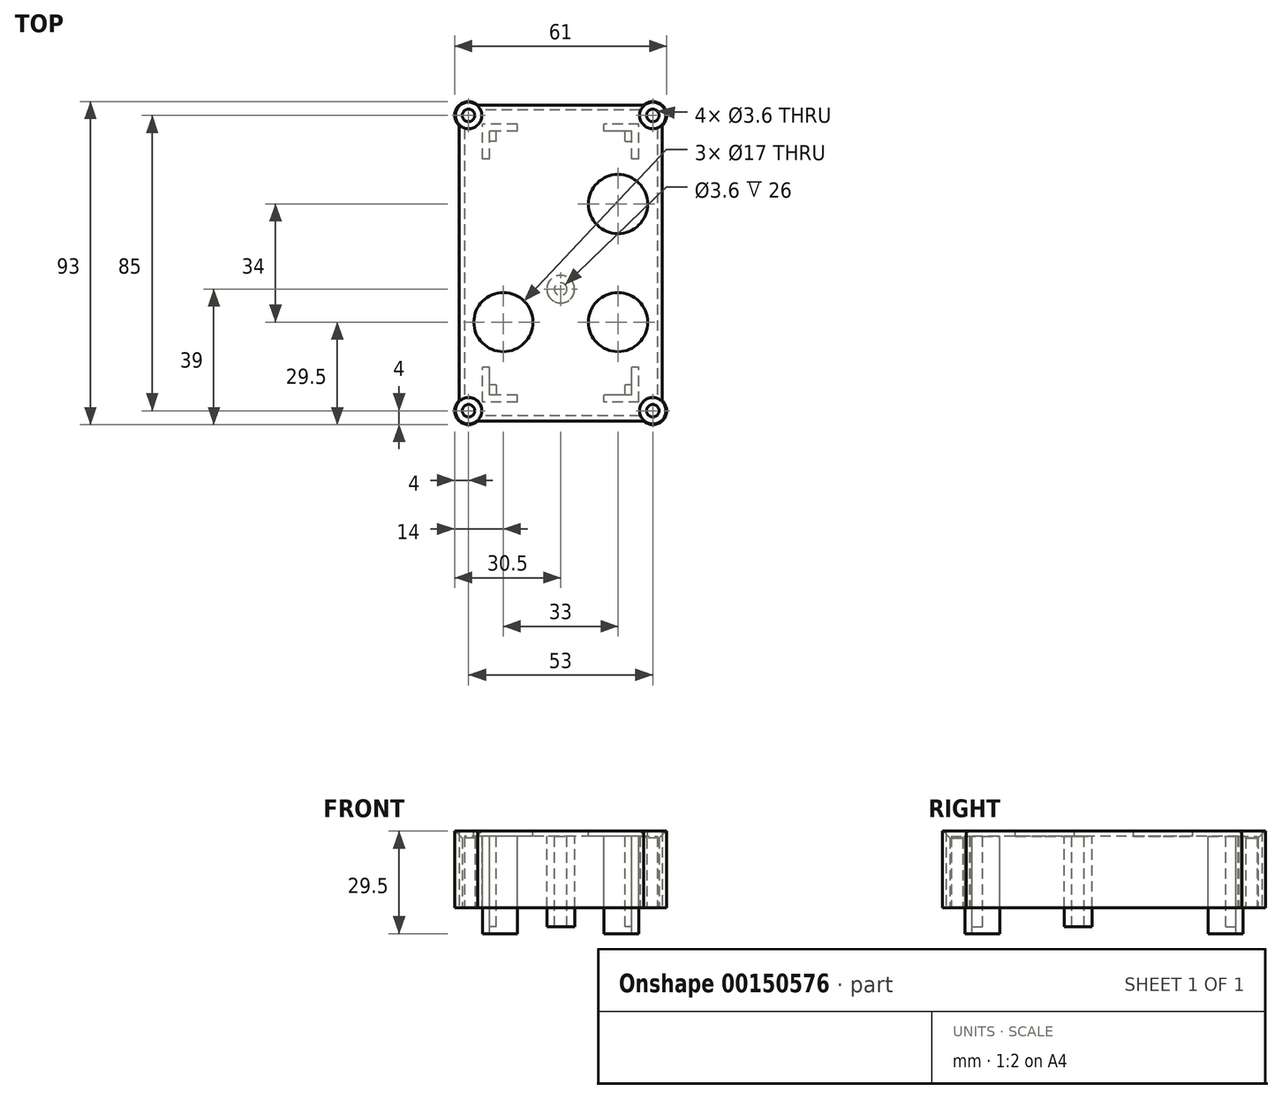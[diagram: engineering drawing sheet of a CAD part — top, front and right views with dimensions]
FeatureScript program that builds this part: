
annotation { "Feature Type Name" : "Feature", "Feature Type Description" : "" }
export const myFeature = defineFeature(function(context is Context, id is Id, definition is map)
    precondition{}
    {
        {
            var Q0;
            Q0=qCreatedBy(makeId("Top.planeOp"),FACE);
            var sketch = newSketch(context, id + "F0", { "sketchPlane" : qUnion([Q0])});
            skLineSegment(sketch, "E0.bottom", {"start": v(29.25, 45.5) * mm, "end": v(-29.25, 45.5) * mm});
            skLineSegment(sketch, "E0.top", {"start": v(29.25, -45.5) * mm, "end": v(-29.25, -45.5) * mm});
            skLineSegment(sketch, "E0.left", {"start": v(29.25, 45.5) * mm, "end": v(29.25, -45.5) * mm});
            skLineSegment(sketch, "E0.right", {"start": v(-29.25, 45.5) * mm, "end": v(-29.25, -45.5) * mm});
            skPoint(sketch, "E0.middle", {"position": v(0, 0) * mm});
            skSolve(sketch);
        }
        {
            var Q0;
            Q0=qSketchRegion(id+"F0",true);
            extrude(context, id + "F1", {"entities" : qUnion([Q0]), "depth" : 22 * mm});
        }
        {
            var Q0;
            Q0=makeQuery(id+"F1.opExtrude","CAP_FACE",FACE,{"disambiguationData":[OSD([sQuery(id+"F0.wireOp",EDGE,"E0.bottom"),sQuery(id+"F0.wireOp",EDGE,"E0.top"),sQuery(id+"F0.wireOp",EDGE,"E0.left"),sQuery(id+"F0.wireOp",EDGE,"E0.right")])],"isStart":true});
            shell(context, id + "F2", {"entities" : qUnion([Q0]), "thickness" : 1.5 * mm});
        }
        {
            var Q0;
            Q0=makeQuery(id+"F1.opExtrude","CAP_FACE",FACE,{"disambiguationData":[OSD([sQuery(id+"F0.wireOp",EDGE,"E0.bottom"),sQuery(id+"F0.wireOp",EDGE,"E0.top"),sQuery(id+"F0.wireOp",EDGE,"E0.left"),sQuery(id+"F0.wireOp",EDGE,"E0.right")])],"isStart":false});
            var sketch = newSketch(context, id + "F3", { "sketchPlane" : qUnion([Q0])});
            skCircle(sketch, "E1", {"center": v(16.5, 17) * mm, "radius": 8.5 * mm});
            skCircle(sketch, "E2.MirrorC", {"center": v(16.5, -17) * mm, "radius": 8.5 * mm});
            skCircle(sketch, "E3.MirrorC", {"center": v(-16.5, -17) * mm, "radius": 8.5 * mm});
            skCircle(sketch, "E4", {"center": v(16.5, -17) * mm, "radius": 11 * mm, "construction": true});
            skCircle(sketch, "E5", {"center": v(-16.5, -17) * mm, "radius": 11 * mm, "construction": true});
            skCircle(sketch, "E6", {"center": v(16.5, 17) * mm, "radius": 11 * mm, "construction": true});
            skSolve(sketch);
        }
        {
            var Q0;
            Q0=qSketchRegion(id+"F3",true);
            extrude(context, id + "F4", {"entities" : qUnion([Q0]), "operationType" : NewBodyOperationType.REMOVE, "oppositeDirection" : true, "depth" : 25 * mm});
        }
        {
            var Q0;
            Q0=makeQuery(id+"F1.opExtrude","SWEPT_EDGE",EDGE,{"disambiguationData":[OSD([sQuery(id+"F0.wireOp",EDGE,"E0.bottom"),sQuery(id+"F0.wireOp",EDGE,"E0.right")])]});
            var Q1;
            Q1=makeQuery(id+"F1.opExtrude","SWEPT_EDGE",EDGE,{"disambiguationData":[OSD([sQuery(id+"F0.wireOp",EDGE,"E0.bottom"),sQuery(id+"F0.wireOp",EDGE,"E0.left")])]});
            var Q2;
            Q2=makeQuery(id+"F1.opExtrude","SWEPT_EDGE",EDGE,{"disambiguationData":[OSD([sQuery(id+"F0.wireOp",EDGE,"E0.top"),sQuery(id+"F0.wireOp",EDGE,"E0.right")])]});
            var Q3;
            Q3=makeQuery(id+"F1.opExtrude","SWEPT_EDGE",EDGE,{"disambiguationData":[OSD([sQuery(id+"F0.wireOp",EDGE,"E0.top"),sQuery(id+"F0.wireOp",EDGE,"E0.left")])]});
            fillet(context, id + "F5", {"entities" : qUnion([Q0, Q1, Q2, Q3]), "radius" : 3 * mm, "tangentPropagation" : true, "allowEdgeOverflow" : false});
        }
        {
            var Q0;
            Q0=makeQuery(id+"F2.opShell","OFFSET_EDGE",EDGE,{"disambiguationData":[OSD([sQuery(id+"F0.wireOp",EDGE,"E0.bottom"),sQuery(id+"F0.wireOp",EDGE,"E0.right")])]});
            var Q1;
            Q1=makeQuery(id+"F2.opShell","OFFSET_EDGE",EDGE,{"disambiguationData":[OSD([sQuery(id+"F0.wireOp",EDGE,"E0.top"),sQuery(id+"F0.wireOp",EDGE,"E0.right")])]});
            var Q2;
            Q2=makeQuery(id+"F2.opShell","OFFSET_EDGE",EDGE,{"disambiguationData":[OSD([sQuery(id+"F0.wireOp",EDGE,"E0.top"),sQuery(id+"F0.wireOp",EDGE,"E0.left")])]});
            var Q3;
            Q3=makeQuery(id+"F2.opShell","OFFSET_EDGE",EDGE,{"disambiguationData":[OSD([sQuery(id+"F0.wireOp",EDGE,"E0.bottom"),sQuery(id+"F0.wireOp",EDGE,"E0.left")])]});
            fillet(context, id + "F6", {"entities" : qUnion([Q0, Q1, Q2, Q3]), "radius" : 2 * mm, "tangentPropagation" : true, "allowEdgeOverflow" : false});
        }
        {
            var Q0;
            Q0=makeQuery(id+"F2.opShell","OFFSET_FACE",FACE,{"disambiguationData":[OSD([sQuery(id+"F0.wireOp",EDGE,"E0.bottom"),sQuery(id+"F0.wireOp",EDGE,"E0.top"),sQuery(id+"F0.wireOp",EDGE,"E0.left"),sQuery(id+"F0.wireOp",EDGE,"E0.right")])]});
            var sketch = newSketch(context, id + "F7", { "sketchPlane" : qUnion([Q0])});
            skLineSegment(sketch, "E7.bottom", {"start": v(20.5, 38) * mm, "end": v(12.5, 38) * mm});
            skLineSegment(sketch, "E7.top", {"start": v(20.5, -38) * mm, "end": v(12.5, -38) * mm});
            skLineSegment(sketch, "E7.left", {"start": v(20.5, 38) * mm, "end": v(20.5, 30) * mm});
            skLineSegment(sketch, "E7.right", {"start": v(-20.5, 38) * mm, "end": v(-20.5, 30) * mm});
            skPoint(sketch, "E7.middle", {"position": v(0, 0) * mm});
            skLineSegment(sketch, "E8.bottom", {"start": v(22.5, 40) * mm, "end": v(12.5, 40) * mm});
            skLineSegment(sketch, "E8.top", {"start": v(22.5, -40) * mm, "end": v(12.5, -40) * mm});
            skLineSegment(sketch, "E8.left", {"start": v(22.5, 40) * mm, "end": v(22.5, 30) * mm});
            skLineSegment(sketch, "E8.right", {"start": v(-22.5, 40) * mm, "end": v(-22.5, 30) * mm});
            skLineSegment(sketch, "E9", {"start": v(12.5, 40) * mm, "end": v(12.5, 38) * mm});
            skLineSegment(sketch, "E10", {"start": v(-12.5, 40) * mm, "end": v(-12.5, 38) * mm});
            skLineSegment(sketch, "E11", {"start": v(22.5, 30) * mm, "end": v(20.5, 30) * mm});
            skLineSegment(sketch, "E12", {"start": v(22.5, -30) * mm, "end": v(20.5, -30) * mm});
            skLineSegment(sketch, "E13.trimOffspring", {"start": v(12.5, -38) * mm, "end": v(12.5, -40) * mm});
            skLineSegment(sketch, "E14.trimOffspring", {"start": v(20.5, -30) * mm, "end": v(20.5, -38) * mm});
            skLineSegment(sketch, "E15.trimOffspring", {"start": v(22.5, -30) * mm, "end": v(22.5, -40) * mm});
            skLineSegment(sketch, "E16.trimOffspring", {"start": v(-12.5, -38) * mm, "end": v(-20.5, -38) * mm});
            skLineSegment(sketch, "E17.trimOffspring", {"start": v(-12.5, -40) * mm, "end": v(-22.5, -40) * mm});
            skLineSegment(sketch, "E18.trimOffspring", {"start": v(-12.5, -38) * mm, "end": v(-12.5, -40) * mm});
            skLineSegment(sketch, "E19.trimOffspring", {"start": v(-20.5, -30) * mm, "end": v(-22.5, -30) * mm});
            skLineSegment(sketch, "E20.trimOffspring", {"start": v(-20.5, -30) * mm, "end": v(-20.5, -38) * mm});
            skLineSegment(sketch, "E21.trimOffspring", {"start": v(-22.5, -30) * mm, "end": v(-22.5, -40) * mm});
            skLineSegment(sketch, "E22.trimOffspring", {"start": v(-20.5, 30) * mm, "end": v(-22.5, 30) * mm});
            skLineSegment(sketch, "E23.trimOffspring", {"start": v(-12.5, 38) * mm, "end": v(-20.5, 38) * mm});
            skLineSegment(sketch, "E24.trimOffspring", {"start": v(-12.5, 40) * mm, "end": v(-22.5, 40) * mm});
            skSolve(sketch);
        }
        {
            var Q0;
            Q0=qSketchRegion(id+"F7",true);
            extrude(context, id + "F8", {"entities" : qUnion([Q0]), "operationType" : NewBodyOperationType.ADD, "depth" : 28 * mm});
        }
        {
            var Q0;
            Q0=makeQuery(id+"F7.imprint","IMPRINT",FACE,{"disambiguationData":[TD([[makeQuery(id+"F7.imprint","IMPRINT",EDGE,{"derivedFrom":sQuery(id+"F7.wireOp",EDGE,"E7.bottom")}),1.0]])]});
            var sketch = newSketch(context, id + "F9", { "sketchPlane" : qUnion([Q0])});
            skCircle(sketch, "E25", {"center": v(0, 7.5) * mm, "radius": 2 * mm, "construction": true});
            skLineSegment(sketch, "E26.bottom", {"start": v(-20.5, 13) * mm, "end": v(-18.5, 13) * mm, "construction": true});
            skLineSegment(sketch, "E26.top", {"start": v(-20.5, 25) * mm, "end": v(-18.5, 25) * mm, "construction": true});
            skLineSegment(sketch, "E26.left", {"start": v(-20.5, 13) * mm, "end": v(-20.5, 25) * mm, "construction": true});
            skLineSegment(sketch, "E26.right", {"start": v(-18.5, 13) * mm, "end": v(-18.5, 25) * mm, "construction": true});
            skLineSegment(sketch, "E27.bottom", {"start": v(20.5, 38) * mm, "end": v(18.5, 38) * mm});
            skLineSegment(sketch, "E27.top", {"start": v(20.5, 35) * mm, "end": v(18.5, 35) * mm});
            skLineSegment(sketch, "E27.left", {"start": v(20.5, 38) * mm, "end": v(20.5, 35) * mm});
            skLineSegment(sketch, "E27.right", {"start": v(18.5, 38) * mm, "end": v(18.5, 35) * mm});
            skLineSegment(sketch, "E28.bottom", {"start": v(-18.5, 35) * mm, "end": v(-20.5, 35) * mm});
            skLineSegment(sketch, "E28.top", {"start": v(-18.5, 38) * mm, "end": v(-20.5, 38) * mm});
            skLineSegment(sketch, "E28.left", {"start": v(-18.5, 35) * mm, "end": v(-18.5, 38) * mm});
            skLineSegment(sketch, "E28.right", {"start": v(-20.5, 35) * mm, "end": v(-20.5, 38) * mm});
            skLineSegment(sketch, "E29.bottom", {"start": v(-18.5, -35) * mm, "end": v(-20.5, -35) * mm});
            skLineSegment(sketch, "E29.top", {"start": v(-18.5, -38) * mm, "end": v(-20.5, -38) * mm});
            skLineSegment(sketch, "E29.left", {"start": v(-18.5, -35) * mm, "end": v(-18.5, -38) * mm});
            skLineSegment(sketch, "E29.right", {"start": v(-20.5, -35) * mm, "end": v(-20.5, -38) * mm});
            skLineSegment(sketch, "E30.bottom", {"start": v(18.5, -35) * mm, "end": v(20.5, -35) * mm});
            skLineSegment(sketch, "E30.top", {"start": v(18.5, -38) * mm, "end": v(20.5, -38) * mm});
            skLineSegment(sketch, "E30.left", {"start": v(18.5, -35) * mm, "end": v(18.5, -38) * mm});
            skLineSegment(sketch, "E30.right", {"start": v(20.5, -35) * mm, "end": v(20.5, -38) * mm});
            skLineSegment(sketch, "E31", {"start": v(-18.5, 38) * mm, "end": v(18.5, 38) * mm});
            skCircle(sketch, "E32", {"center": v(0, 7.5) * mm, "radius": 4 * mm});
            skCircle(sketch, "E33", {"center": v(0, 7.5) * mm, "radius": 1.8 * mm});
            skLineSegment(sketch, "E34", {"start": v(-18.5, 18) * mm, "end": v(-14.55, 18) * mm, "construction": true});
            skLineSegment(sketch, "E35", {"start": v(-14.55, 18) * mm, "end": v(-14.6, 20) * mm, "construction": true});
            skLineSegment(sketch, "E36", {"start": v(-14.6, 20) * mm, "end": v(-18.5, 20) * mm, "construction": true});
            skSolve(sketch);
        }
        {
            var Q0;
            Q0=qSketchRegion(id+"F9",true);
            extrude(context, id + "F10", {"entities" : qUnion([Q0]), "operationType" : NewBodyOperationType.ADD, "depth" : 26 * mm});
        }
        {
            var Q0;
            Q0=makeQuery(id+"F0.imprint","IMPRINT",FACE,{"disambiguationData":[TD([[makeQuery(id+"F0.imprint","IMPRINT",EDGE,{"derivedFrom":sQuery(id+"F0.wireOp",EDGE,"E0.bottom")}),1.0]])]});
            var sketch = newSketch(context, id + "F11", { "sketchPlane" : qUnion([Q0])});
            skLineSegment(sketch, "E37", {"start": v(26.5, -42.5) * mm, "end": v(26.5, 42.5) * mm, "construction": true});
            skLineSegment(sketch, "E38", {"start": v(-26.5, 42.5) * mm, "end": v(-26.5, -42.5) * mm, "construction": true});
            skLineSegment(sketch, "E39", {"start": v(26.5, -42.5) * mm, "end": v(-26.5, -42.5) * mm, "construction": true});
            skLineSegment(sketch, "E40", {"start": v(26.5, 42.5) * mm, "end": v(-26.5, 42.5) * mm, "construction": true});
            skCircle(sketch, "E41", {"center": v(26.5, -42.5) * mm, "radius": 4 * mm});
            skCircle(sketch, "E42", {"center": v(26.5, 42.5) * mm, "radius": 4 * mm});
            skCircle(sketch, "E43", {"center": v(-26.5, 42.5) * mm, "radius": 4 * mm});
            skCircle(sketch, "E44", {"center": v(-26.5, -42.5) * mm, "radius": 4 * mm});
            skSolve(sketch);
        }
        {
            var Q0;
            Q0=qSketchRegion(id+"F11",true);
            extrude(context, id + "F12", {"entities" : qUnion([Q0]), "operationType" : NewBodyOperationType.ADD, "depth" : 22 * mm});
        }
        {
            var Q0;
            Q0=qCreatedBy(makeId("Top.planeOp"),FACE);
            var sketch = newSketch(context, id + "F13", { "sketchPlane" : qUnion([Q0])});
            skCircle(sketch, "E45", {"center": v(26.5, -42.5) * mm, "radius": 1.8 * mm});
            skCircle(sketch, "E46", {"center": v(26.5, 42.5) * mm, "radius": 1.8 * mm});
            skCircle(sketch, "E47", {"center": v(-26.5, -42.5) * mm, "radius": 1.8 * mm});
            skCircle(sketch, "E48", {"center": v(-26.5, 42.5) * mm, "radius": 1.8 * mm});
            skSolve(sketch);
        }
        {
            var Q0;
            Q0=qSketchRegion(id+"F13",true);
            extrude(context, id + "F14", {"entities" : qUnion([Q0]), "operationType" : NewBodyOperationType.REMOVE, "depth" : 26 * mm});
        }
        {
            var Q0;
            Q0=makeQuery(id+"F0.imprint","IMPRINT",FACE,{"disambiguationData":[TD([[makeQuery(id+"F0.imprint","IMPRINT",EDGE,{"derivedFrom":sQuery(id+"F0.wireOp",EDGE,"E0.bottom")}),1.0]])]});
            var sketch = newSketch(context, id + "F15", { "sketchPlane" : qUnion([Q0])});
            skArc(sketch, "E49", {"start": v(27.75, -37.9) * mm, "mid": v(21.78, -38.03) * mm, "end": v(21.9, -44) * mm, "construction": true});
            skArc(sketch, "E50", {"start": v(21.9, 44) * mm, "mid": v(21.78, 38.03) * mm, "end": v(27.75, 37.9) * mm, "construction": true});
            skArc(sketch, "E51", {"start": v(-25.85, 35.82) * mm, "mid": v(-19.79, 37.94) * mm, "end": v(-21.9, 44) * mm, "construction": true});
            skArc(sketch, "E52", {"start": v(-21.9, -44) * mm, "mid": v(-22.32, -40.44) * mm, "end": v(-25.85, -39.82) * mm, "construction": true});
            skLineSegment(sketch, "E53", {"start": v(-25.85, -39.82) * mm, "end": v(-25.85, 35.82) * mm, "construction": true});
            skLineSegment(sketch, "E54", {"start": v(-21.9, 44) * mm, "end": v(21.9, 44) * mm, "construction": true});
            skLineSegment(sketch, "E55", {"start": v(27.75, -37.9) * mm, "end": v(27.75, 37.9) * mm, "construction": true});
            skLineSegment(sketch, "E56", {"start": v(21.9, -44) * mm, "end": v(-21.9, -44) * mm, "construction": true});
            skSolve(sketch);
        }
        {
            var Q0;
            Q0=makeQuery(id+"F14.boolean.opBoolean","INTERSECT",EDGE,{"derivedFrom":[makeQuery(id+"F12.boolean.opBoolean","MERGE",FACE,{"derivedFrom":[makeQuery(id+"F1.opExtrude","CAP_FACE",FACE,{"disambiguationData":[OSD([sQuery(id+"F0.wireOp",EDGE,"E0.bottom"),sQuery(id+"F0.wireOp",EDGE,"E0.top"),sQuery(id+"F0.wireOp",EDGE,"E0.left"),sQuery(id+"F0.wireOp",EDGE,"E0.right")])],"isStart":false}),makeQuery(id+"F12.opExtrude","CAP_FACE",FACE,{"disambiguationData":[OSD([sQuery(id+"F11.wireOp",EDGE,"E41")])],"isStart":false}),makeQuery(id+"F12.opExtrude","CAP_FACE",FACE,{"disambiguationData":[OSD([sQuery(id+"F11.wireOp",EDGE,"E42")])],"isStart":false}),makeQuery(id+"F12.opExtrude","CAP_FACE",FACE,{"disambiguationData":[OSD([sQuery(id+"F11.wireOp",EDGE,"E43")])],"isStart":false}),makeQuery(id+"F12.opExtrude","CAP_FACE",FACE,{"disambiguationData":[OSD([sQuery(id+"F11.wireOp",EDGE,"E44")])],"isStart":false})]}),makeQuery(id+"F14.opExtrude","SWEPT_FACE",FACE,{"disambiguationData":[OSD([sQuery(id+"F13.wireOp",EDGE,"E45")])]})]});
            var Q1;
            Q1=makeQuery(id+"F14.boolean.opBoolean","INTERSECT",EDGE,{"derivedFrom":[makeQuery(id+"F12.boolean.opBoolean","MERGE",FACE,{"derivedFrom":[makeQuery(id+"F1.opExtrude","CAP_FACE",FACE,{"disambiguationData":[OSD([sQuery(id+"F0.wireOp",EDGE,"E0.bottom"),sQuery(id+"F0.wireOp",EDGE,"E0.top"),sQuery(id+"F0.wireOp",EDGE,"E0.left"),sQuery(id+"F0.wireOp",EDGE,"E0.right")])],"isStart":false}),makeQuery(id+"F12.opExtrude","CAP_FACE",FACE,{"disambiguationData":[OSD([sQuery(id+"F11.wireOp",EDGE,"E41")])],"isStart":false}),makeQuery(id+"F12.opExtrude","CAP_FACE",FACE,{"disambiguationData":[OSD([sQuery(id+"F11.wireOp",EDGE,"E42")])],"isStart":false}),makeQuery(id+"F12.opExtrude","CAP_FACE",FACE,{"disambiguationData":[OSD([sQuery(id+"F11.wireOp",EDGE,"E43")])],"isStart":false}),makeQuery(id+"F12.opExtrude","CAP_FACE",FACE,{"disambiguationData":[OSD([sQuery(id+"F11.wireOp",EDGE,"E44")])],"isStart":false})]}),makeQuery(id+"F14.opExtrude","SWEPT_FACE",FACE,{"disambiguationData":[OSD([sQuery(id+"F13.wireOp",EDGE,"E46")])]})]});
            var Q2;
            Q2=makeQuery(id+"F14.boolean.opBoolean","INTERSECT",EDGE,{"derivedFrom":[makeQuery(id+"F12.boolean.opBoolean","MERGE",FACE,{"derivedFrom":[makeQuery(id+"F1.opExtrude","CAP_FACE",FACE,{"disambiguationData":[OSD([sQuery(id+"F0.wireOp",EDGE,"E0.bottom"),sQuery(id+"F0.wireOp",EDGE,"E0.top"),sQuery(id+"F0.wireOp",EDGE,"E0.left"),sQuery(id+"F0.wireOp",EDGE,"E0.right")])],"isStart":false}),makeQuery(id+"F12.opExtrude","CAP_FACE",FACE,{"disambiguationData":[OSD([sQuery(id+"F11.wireOp",EDGE,"E41")])],"isStart":false}),makeQuery(id+"F12.opExtrude","CAP_FACE",FACE,{"disambiguationData":[OSD([sQuery(id+"F11.wireOp",EDGE,"E42")])],"isStart":false}),makeQuery(id+"F12.opExtrude","CAP_FACE",FACE,{"disambiguationData":[OSD([sQuery(id+"F11.wireOp",EDGE,"E43")])],"isStart":false}),makeQuery(id+"F12.opExtrude","CAP_FACE",FACE,{"disambiguationData":[OSD([sQuery(id+"F11.wireOp",EDGE,"E44")])],"isStart":false})]}),makeQuery(id+"F14.opExtrude","SWEPT_FACE",FACE,{"disambiguationData":[OSD([sQuery(id+"F13.wireOp",EDGE,"E48")])]})]});
            var Q3;
            Q3=makeQuery(id+"F14.boolean.opBoolean","INTERSECT",EDGE,{"derivedFrom":[makeQuery(id+"F12.boolean.opBoolean","MERGE",FACE,{"derivedFrom":[makeQuery(id+"F1.opExtrude","CAP_FACE",FACE,{"disambiguationData":[OSD([sQuery(id+"F0.wireOp",EDGE,"E0.bottom"),sQuery(id+"F0.wireOp",EDGE,"E0.top"),sQuery(id+"F0.wireOp",EDGE,"E0.left"),sQuery(id+"F0.wireOp",EDGE,"E0.right")])],"isStart":false}),makeQuery(id+"F12.opExtrude","CAP_FACE",FACE,{"disambiguationData":[OSD([sQuery(id+"F11.wireOp",EDGE,"E41")])],"isStart":false}),makeQuery(id+"F12.opExtrude","CAP_FACE",FACE,{"disambiguationData":[OSD([sQuery(id+"F11.wireOp",EDGE,"E42")])],"isStart":false}),makeQuery(id+"F12.opExtrude","CAP_FACE",FACE,{"disambiguationData":[OSD([sQuery(id+"F11.wireOp",EDGE,"E43")])],"isStart":false}),makeQuery(id+"F12.opExtrude","CAP_FACE",FACE,{"disambiguationData":[OSD([sQuery(id+"F11.wireOp",EDGE,"E44")])],"isStart":false})]}),makeQuery(id+"F14.opExtrude","SWEPT_FACE",FACE,{"disambiguationData":[OSD([sQuery(id+"F13.wireOp",EDGE,"E47")])]})]});
            chamfer(context, id + "F16", {"entities" : qUnion([Q0, Q1, Q2, Q3]), "width" : 2 * mm, "tangentPropagation" : true});
        }
    });
